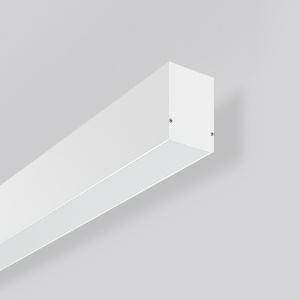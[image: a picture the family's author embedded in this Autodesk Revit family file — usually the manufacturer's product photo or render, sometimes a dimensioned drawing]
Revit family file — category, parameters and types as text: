
# Revit family: less_is_more_50_312608_002_76_7bf2
name_source: partatom
category: Lighting Fixtures
units: mm (PartAtom-declared; Revit-internal decimal feet)

## family parameters
Cut with Voids When Loaded = No
Host = Face
Light Source = No
Part Type = Normal
Room Calculation Point = No
Round Connector Dimension = Use Diameter
Shared = No

## types (1)
- LESS IS MORE 50 (1 x LED Modul 830, 2600 lm, 3000)
    Apparent Load = 20 VA
    CIE Flux Codes = 48 80 96 50 100
    Color Rendering = 80
    Color Temperature = 3000
    Default Elevation = 1800 mm
    Description = Series: LESS IS MORE 50
Linear wall luminaires. Housing: extruded aluminium profile, powder-coated. End cap aluminium powder-coated. Diffuser made of non-yellowing plastic (PMMA), opal. Direct 50%, indirect 50% light emission. Suitable for Wall (surface). LED unit with integrated converter interchangeable and removable. Suitable for through-wiring. With sensors or as a safety luminaire on request. 
Colour: traffic white, matt (RAL 9016)
Length: 1127 mm
Width: 67 mm
Height: 75 mm
Lamp: LED
Socket: without socket
Colour temperature: 3000K
Colour rendering index (CRI): 80
Light source: LED
Socket lamp2: Without base
Colour temperature: 3000K
Colour rendering index (CRI) 2: 80
System power: 20 W
Rated luminous flux: 2600 lm
Luminous efficiency: 130 lm/W
Control gear: Converter, dimmable, DALI
Control gear: Converter, dimmable, DALI
Protection class: I
Type of protection: IP 20
    Height = 75 mm
    Lamp = 1 x LED Modul 830
    Lamp Light Flux = 2600 lm
    Lamp count = 1
    Length = 1127 mm
    Lifetime = 50000 h
    Luminous efficacy = 130 lm/W
    Manufacturer = RZB
    ModVariant = No
    Model = 312608.002.76
    Mounting Place = Wall
    Mounting Type = Surface mounted
    Number of Poles = 1
    OnlyDefault = Yes
    Power Factor = 1
    Product Name = LESS IS MORE 50
    Product group = Surface mounted LED linear luminaires
    ProductGroupID = 2007
    Protection Class = Protection class I
    Protection Degree = IP 20
    RLX_Detail_Level = 1
    RLX_Emergency_Light_Flux = 0 lm
    RLX_Emergency_Type = 0
    RLX_Emergency_Type_DB = No
    RlxData = <blob elided: 39597 chars, md5=44b88732>
    Socket = socket
    Standby Power = 0 W
    System Light Flux = 2600 lm
    System Power = 20 W
    Type Comments = Product without accessories
    Type Image = 312606.002.jpg
    URL = http://relux.com
    VarID = ---
    Voltage = 0 V
    Weight = 0.00 kg
    Width = 67 mm

## geometry (parser evidence)
native form markers: Blend x4, Sweep x11
no freeform markers — native parametric forms only
